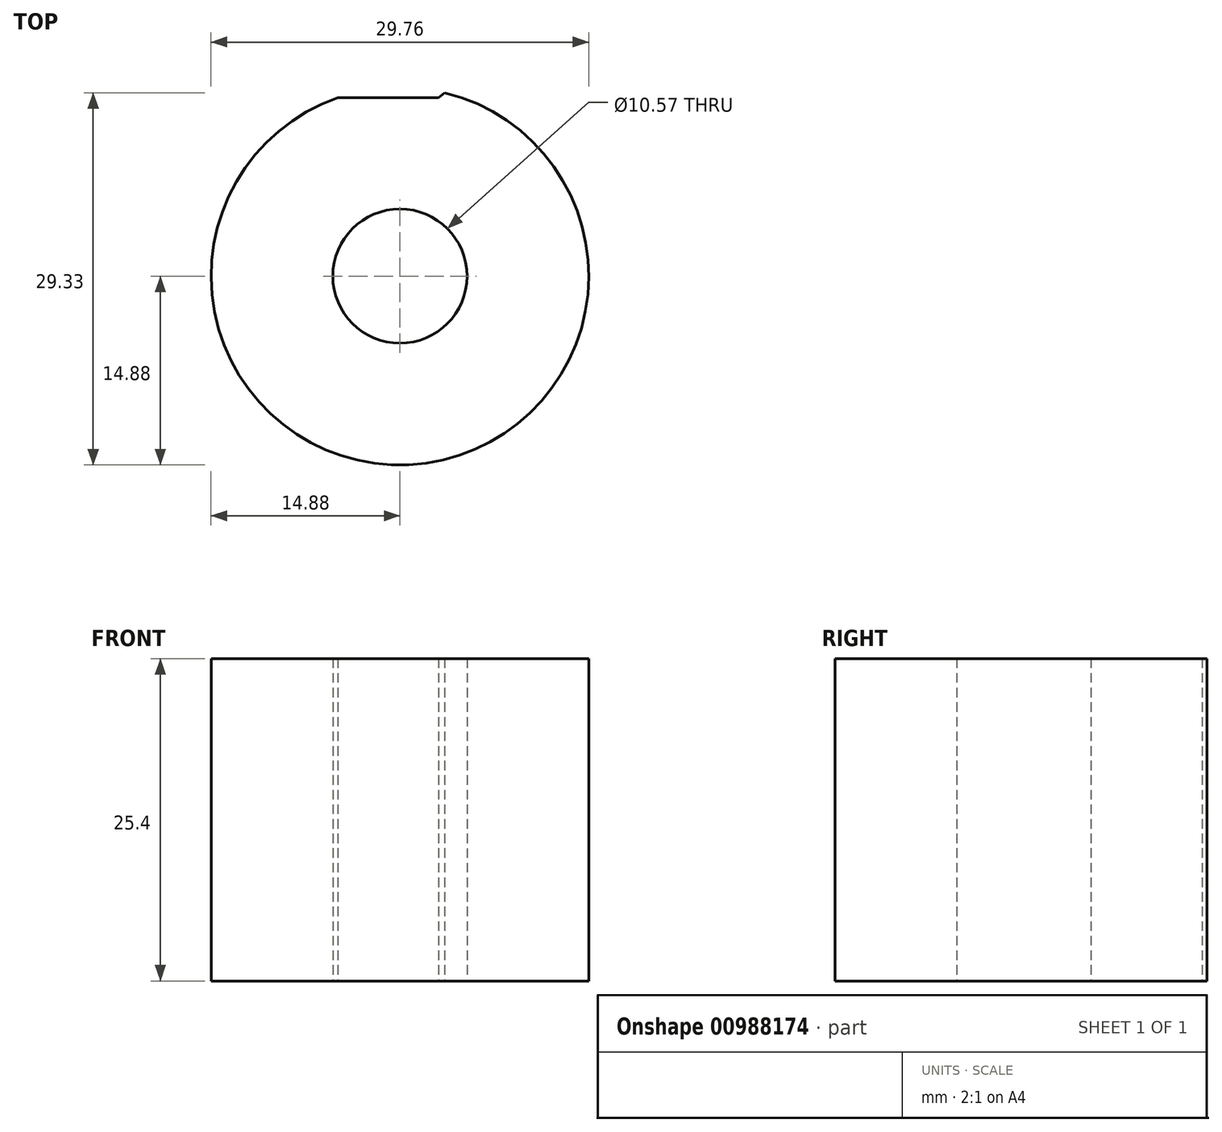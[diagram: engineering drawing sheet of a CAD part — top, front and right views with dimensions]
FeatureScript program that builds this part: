
annotation { "Feature Type Name" : "Feature", "Feature Type Description" : "" }
export const myFeature = defineFeature(function(context is Context, id is Id, definition is map)
    precondition{}
    {
        {
            var Q0;
            Q0=qCreatedBy(makeId("Top.planeOp"),FACE);
            var sketch = newSketch(context, id + "F0", { "sketchPlane" : qUnion([Q0])});
            skCircle(sketch, "E0", {"center": v(0, 0) * mm, "radius": 14.88 * mm});
            skCircle(sketch, "E1", {"center": v(0, 0) * mm, "radius": 5.29 * mm});
            skSolve(sketch);
        }
        {
            var Q0;
            Q0=makeQuery(id+"F0.imprint","IMPRINT",FACE,{"disambiguationData":[TD([[makeQuery(id+"F0.imprint","IMPRINT",EDGE,{"derivedFrom":sQuery(id+"F0.wireOp",EDGE,"E0")}),1.0]])]});
            var sketch = newSketch(context, id + "F1", { "sketchPlane" : qUnion([Q0])});
            skLineSegment(sketch, "E2", {"start": v(-5.13, 14.05) * mm, "end": v(-5.13, -10.92) * mm});
            skLineSegment(sketch, "E3", {"start": v(3.7, 14.58) * mm, "end": v(3.7, -11.56) * mm});
            skLineSegment(sketch, "E4", {"start": v(-5.13, 14.05) * mm, "end": v(3.05, 14.05) * mm});
            skLineSegment(sketch, "E5", {"start": v(3.05, 14.05) * mm, "end": v(-5.13, 14.05) * mm});
            skLineSegment(sketch, "E6", {"start": v(-4.76, -10.92) * mm, "end": v(3.7, -11.56) * mm});
            skLineSegment(sketch, "E7", {"start": v(-4.76, -10.92) * mm, "end": v(-5.13, -10.92) * mm});
            skLineSegment(sketch, "E8", {"start": v(3.05, 14.05) * mm, "end": v(3.7, 14.58) * mm});
            skSolve(sketch);
        }
        {
            var Q0;
            {var subQ0=sQuery(id+"F1.wireOp",EDGE,"E8");var subQ1=sQuery(id+"F1.wireOp",EDGE,"E5");var subQ2=makeQuery(id+"F1.imprint","INTERSECT",VERTEX,{"derivedFrom":[subQ1,subQ0]});Q0=makeQuery(id+"F1.imprint","IMPRINT",FACE,{"disambiguationData":[TD([[makeQuery(id+"F1.imprint","IMPRINT",EDGE,{"disambiguationData":[TD([[subQ2,-1.0]])],"derivedFrom":subQ1}),-1.0]])]});}
            var Q1;
            {var subQ3=makeQuery(id+"F0.imprint","IMPRINT",EDGE,{"derivedFrom":sQuery(id+"F0.wireOp",EDGE,"E0")});var subQ5=sQuery(id+"F1.wireOp",EDGE,"E2");var subQ6=makeQuery(id+"F1.imprint","INTERSECT",VERTEX,{"derivedFrom":[subQ3,subQ5]});Q1=makeQuery(id+"F1.imprint","IMPRINT",FACE,{"disambiguationData":[TD([[makeQuery(id+"F1.imprint","IMPRINT",EDGE,{"disambiguationData":[TD([[subQ6,-1.0]])],"derivedFrom":subQ5}),1.0]])]});}
            var Q2;
            {var subQ0=sQuery(id+"F1.wireOp",EDGE,"E6");Q2=makeQuery(id+"F1.imprint","IMPRINT",FACE,{"disambiguationData":[TD([[makeQuery(id+"F1.imprint","IMPRINT",EDGE,{"derivedFrom":subQ0}),-1.0]])]});}
            var Q3;
            {var subQ1=sQuery(id+"F1.wireOp",EDGE,"E6");Q3=makeQuery(id+"F1.imprint","IMPRINT",FACE,{"disambiguationData":[TD([[makeQuery(id+"F1.imprint","IMPRINT",EDGE,{"derivedFrom":subQ1}),1.0]])]});}
            extrude(context, id + "F2", {"entities" : qUnion([Q0, Q1, Q2, Q3]), "depth" : 25.4 * mm, "offsetDistance" : 25.4 * mm});
        }
    });
